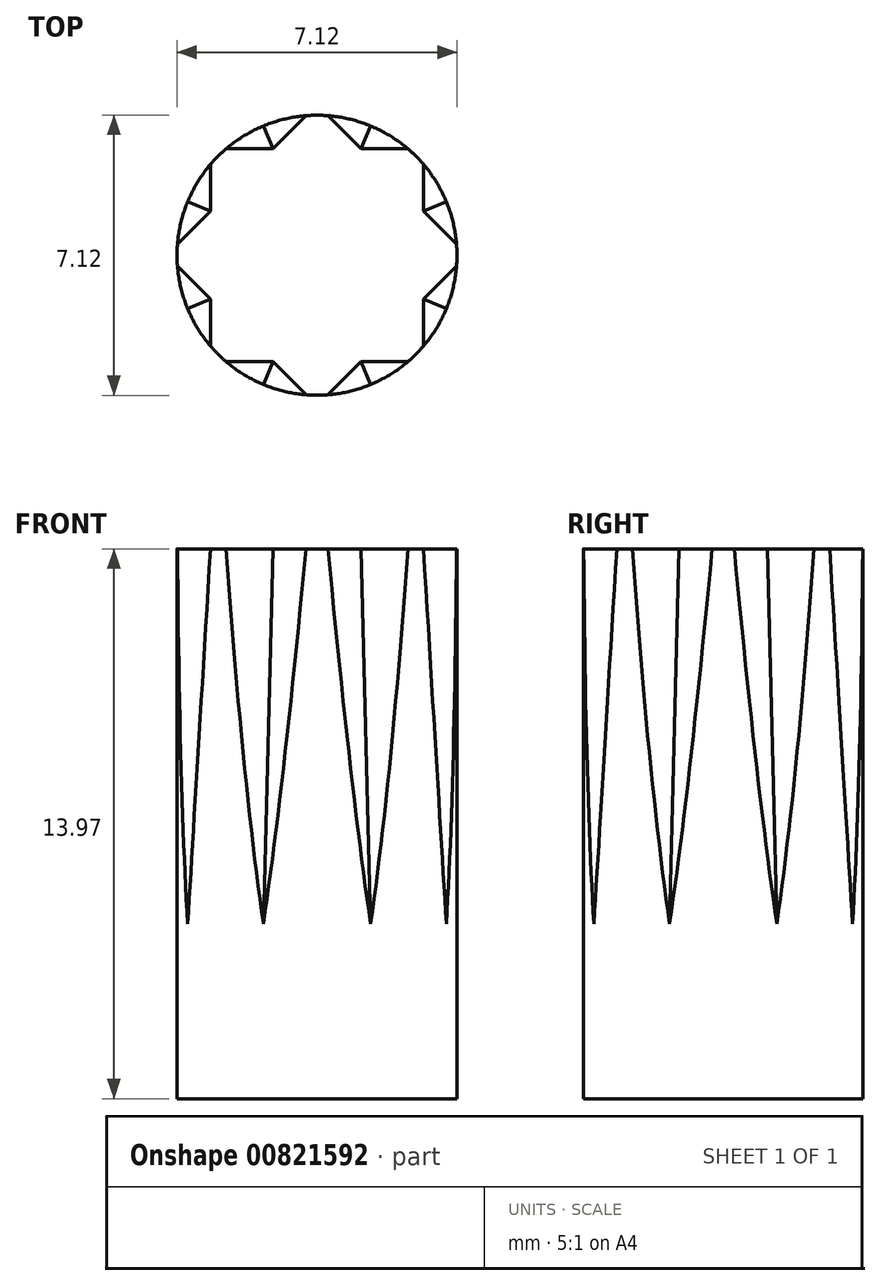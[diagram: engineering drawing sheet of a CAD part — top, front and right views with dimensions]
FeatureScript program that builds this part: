
annotation { "Feature Type Name" : "Feature", "Feature Type Description" : "" }
export const myFeature = defineFeature(function(context is Context, id is Id, definition is map)
    precondition{}
    {
        {
            var Q0;
            Q0=qCreatedBy(makeId("Top.planeOp"),FACE);
            var sketch = newSketch(context, id + "F0", { "sketchPlane" : qUnion([Q0])});
            skLineSegment(sketch, "E0.bottom", {"start": v(3.56, -3.56) * mm, "end": v(-3.56, -3.56) * mm});
            skLineSegment(sketch, "E0.top", {"start": v(3.56, 3.56) * mm, "end": v(-3.56, 3.56) * mm});
            skLineSegment(sketch, "E0.left", {"start": v(3.56, -3.56) * mm, "end": v(3.56, 3.56) * mm});
            skLineSegment(sketch, "E0.right", {"start": v(-3.56, -3.56) * mm, "end": v(-3.56, 3.56) * mm});
            skPoint(sketch, "E0.middle", {"position": v(0, 0) * mm});
            skLineSegment(sketch, "E1.bottom", {"start": v(5.03, 0) * mm, "end": v(0, -5.03) * mm});
            skLineSegment(sketch, "E1.top", {"start": v(0, 5.03) * mm, "end": v(-5.03, 0) * mm});
            skLineSegment(sketch, "E1.left", {"start": v(5.03, 0) * mm, "end": v(0, 5.03) * mm});
            skLineSegment(sketch, "E1.right", {"start": v(0, -5.03) * mm, "end": v(-5.03, 0) * mm});
            skLineSegment(sketch, "E2", {"start": v(-3.56, 1.47) * mm, "end": v(3.56, -1.47) * mm, "construction": true});
            skLineSegment(sketch, "E3", {"start": v(3.56, 1.47) * mm, "end": v(-3.56, -1.47) * mm, "construction": true});
            skLineSegment(sketch, "E4", {"start": v(1.47, 3.56) * mm, "end": v(-1.47, -3.56) * mm, "construction": true});
            skLineSegment(sketch, "E5", {"start": v(-1.47, 3.56) * mm, "end": v(1.47, -3.56) * mm, "construction": true});
            skSolve(sketch);
        }
        {
            var Q0;
            {var subQ5=sQuery(id+"F0.wireOp",EDGE,"E1.bottom");var subQ13=sQuery(id+"F0.wireOp",EDGE,"E0.bottom");var subQ14=makeQuery(id+"F0.imprint","INTERSECT",VERTEX,{"derivedFrom":[subQ13,subQ5]});Q0=makeQuery(id+"F0.imprint","IMPRINT",FACE,{"disambiguationData":[TD([[makeQuery(id+"F0.imprint","IMPRINT",EDGE,{"disambiguationData":[TD([[subQ14,-1.0]])],"derivedFrom":subQ13}),-1.0]])]});}
            cPlane(context, id + "F1", {"entities" : qUnion([Q0]), "cplaneType" : CPlaneType.OFFSET, "offset" : 13.97 * mm, "width" : 152.4 * mm, "height" : 152.4 * mm});
        }
        {
            var Q0;
            Q0=qCreatedBy(id+"F1.planeOp",FACE);
            var sketch = newSketch(context, id + "F2", { "sketchPlane" : qUnion([Q0])});
            skLineSegment(sketch, "E6.bottom", {"start": v(2.7, -2.7) * mm, "end": v(-2.7, -2.7) * mm});
            skLineSegment(sketch, "E6.top", {"start": v(2.7, 2.7) * mm, "end": v(-2.7, 2.7) * mm});
            skLineSegment(sketch, "E6.left", {"start": v(2.7, -2.7) * mm, "end": v(2.7, 2.7) * mm});
            skLineSegment(sketch, "E6.right", {"start": v(-2.7, -2.7) * mm, "end": v(-2.7, 2.7) * mm});
            skPoint(sketch, "E6.middle", {"position": v(0, 0) * mm});
            skLineSegment(sketch, "E7.bottom", {"start": v(0, -3.83) * mm, "end": v(-3.83, 0) * mm});
            skLineSegment(sketch, "E7.top", {"start": v(3.83, 0) * mm, "end": v(0, 3.83) * mm});
            skLineSegment(sketch, "E7.left", {"start": v(0, -3.83) * mm, "end": v(3.83, 0) * mm});
            skLineSegment(sketch, "E7.right", {"start": v(-3.83, 0) * mm, "end": v(0, 3.83) * mm});
            skSolve(sketch);
        }
        {
            var Q0;
            Q0 = qSketchRegion(id + "F2", true);
            var Q1;
            Q1 = qSketchRegion(id + "F0", true);
            loft(context, id + "F3", {"sheetProfilesArray" : [{ "sheetProfileEntities" : qUnion([Q0]) }, { "sheetProfileEntities" : qUnion([Q1]) }]});
        }
        {
            var Q0;
            Q0=qCreatedBy(makeId("Top.planeOp"),FACE);
            var sketch = newSketch(context, id + "F4", { "sketchPlane" : qUnion([Q0])});
            skCircle(sketch, "E8", {"center": v(0, 0) * mm, "radius": 3.56 * mm});
            skCircle(sketch, "E9", {"center": v(0, 0) * mm, "radius": 7.14 * mm});
            skSolve(sketch);
        }
        {
            var Q0;
            Q0 = qSketchRegion(id + "F4", true);
            extrude(context, id + "F5", {"entities" : qUnion([Q0]), "operationType" : NewBodyOperationType.REMOVE, "depth" : 25.4 * mm, "offsetDistance" : 25.4 * mm});
        }
    });
